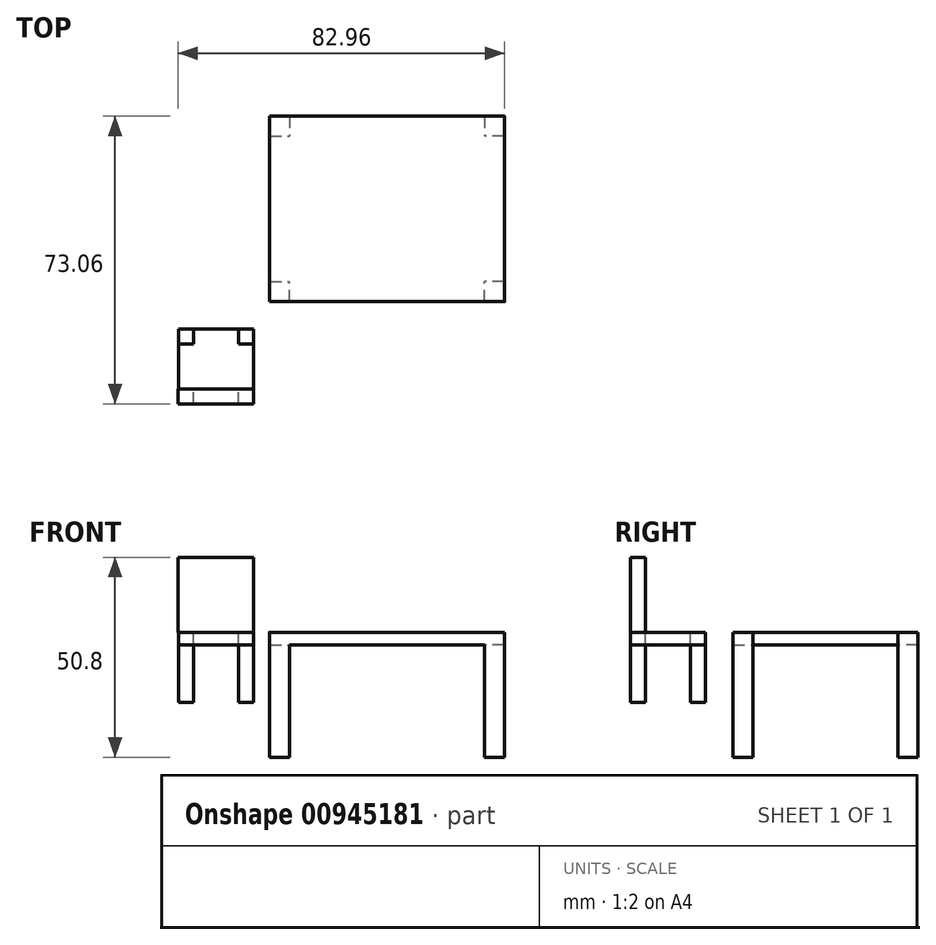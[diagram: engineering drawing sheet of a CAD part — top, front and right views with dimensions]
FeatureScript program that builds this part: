
annotation { "Feature Type Name" : "Feature", "Feature Type Description" : "" }
export const myFeature = defineFeature(function(context is Context, id is Id, definition is map)
    precondition{}
    {
        {
            var Q0;
            Q0=qCreatedBy(makeId("Top.planeOp"),FACE);
            var sketch = newSketch(context, id + "F0", { "sketchPlane" : qUnion([Q0])});
            skLineSegment(sketch, "E0.bottom", {"start": v(-29.83, 23.55) * mm, "end": v(29.83, 23.55) * mm});
            skLineSegment(sketch, "E0.top", {"start": v(-29.83, -23.55) * mm, "end": v(29.83, -23.55) * mm});
            skLineSegment(sketch, "E0.left", {"start": v(-29.83, 23.55) * mm, "end": v(-29.83, -23.55) * mm});
            skLineSegment(sketch, "E0.right", {"start": v(29.83, 23.55) * mm, "end": v(29.83, -23.55) * mm});
            skPoint(sketch, "E0.middle", {"position": v(0, 0) * mm});
            skSolve(sketch);
        }
        {
            var Q0;
            Q0=makeQuery(id+"F0.imprint","IMPRINT",FACE,{"disambiguationData":[TD([[makeQuery(id+"F0.imprint","IMPRINT",EDGE,{"derivedFrom":sQuery(id+"F0.wireOp",EDGE,"E0.bottom")}),-1.0]])]});
            extrude(context, id + "F1", {"entities" : qUnion([Q0]), "depth" : -3.17 * mm, "offsetDistance" : 25.4 * mm});
        }
        {
            var Q0;
            Q0=qCreatedBy(makeId("Top.planeOp"),FACE);
            var sketch = newSketch(context, id + "F2", { "sketchPlane" : qUnion([Q0])});
            skLineSegment(sketch, "E1.bottom", {"start": v(29.87, -23.54) * mm, "end": v(24.79, -23.54) * mm});
            skLineSegment(sketch, "E1.top", {"start": v(29.87, -18.46) * mm, "end": v(24.79, -18.46) * mm});
            skLineSegment(sketch, "E1.left", {"start": v(29.87, -23.54) * mm, "end": v(29.87, -18.46) * mm});
            skLineSegment(sketch, "E1.right", {"start": v(24.79, -23.54) * mm, "end": v(24.79, -18.46) * mm});
            skLineSegment(sketch, "E2.MirrorCS", {"start": v(29.87, 23.54) * mm, "end": v(24.79, 23.54) * mm});
            skLineSegment(sketch, "E3.MirrorCS", {"start": v(24.79, 23.54) * mm, "end": v(24.79, 18.46) * mm});
            skLineSegment(sketch, "E4.MirrorCS", {"start": v(29.87, 18.46) * mm, "end": v(24.79, 18.46) * mm});
            skLineSegment(sketch, "E5.MirrorCS", {"start": v(29.87, 23.54) * mm, "end": v(29.87, 18.46) * mm});
            skLineSegment(sketch, "E6.MirrorCS", {"start": v(-24.79, 23.54) * mm, "end": v(-24.79, 18.46) * mm});
            skLineSegment(sketch, "E7.MirrorCS", {"start": v(-29.87, 18.46) * mm, "end": v(-24.79, 18.46) * mm});
            skLineSegment(sketch, "E8.MirrorCS", {"start": v(-29.87, 23.54) * mm, "end": v(-29.87, 18.46) * mm});
            skLineSegment(sketch, "E9.MirrorCS", {"start": v(-29.87, 23.54) * mm, "end": v(-24.79, 23.54) * mm});
            skLineSegment(sketch, "E10.MirrorCS", {"start": v(-24.79, -23.54) * mm, "end": v(-24.79, -18.46) * mm});
            skLineSegment(sketch, "E11.MirrorCS", {"start": v(-29.87, -23.54) * mm, "end": v(-24.79, -23.54) * mm});
            skLineSegment(sketch, "E12.MirrorCS", {"start": v(-29.87, -23.54) * mm, "end": v(-29.87, -18.46) * mm});
            skLineSegment(sketch, "E13.MirrorCS", {"start": v(-29.87, -18.46) * mm, "end": v(-24.79, -18.46) * mm});
            skSolve(sketch);
        }
        {
            var Q0;
            Q0=makeQuery(id+"F2.imprint","IMPRINT",FACE,{"disambiguationData":[TD([[makeQuery(id+"F2.imprint","IMPRINT",EDGE,{"derivedFrom":sQuery(id+"F2.wireOp",EDGE,"E6.MirrorCS")}),-1.0]])]});
            var Q1;
            Q1=makeQuery(id+"F2.imprint","IMPRINT",FACE,{"disambiguationData":[TD([[makeQuery(id+"F2.imprint","IMPRINT",EDGE,{"derivedFrom":sQuery(id+"F2.wireOp",EDGE,"E10.MirrorCS")}),1.0]])]});
            var Q2;
            Q2=makeQuery(id+"F2.imprint","IMPRINT",FACE,{"disambiguationData":[TD([[makeQuery(id+"F2.imprint","IMPRINT",EDGE,{"derivedFrom":sQuery(id+"F2.wireOp",EDGE,"E1.bottom")}),-1.0]])]});
            var Q3;
            Q3=makeQuery(id+"F2.imprint","IMPRINT",FACE,{"disambiguationData":[TD([[makeQuery(id+"F2.imprint","IMPRINT",EDGE,{"derivedFrom":sQuery(id+"F2.wireOp",EDGE,"E2.MirrorCS")}),1.0]])]});
            extrude(context, id + "F3", {"entities" : qUnion([Q0, Q1, Q2, Q3]), "operationType" : NewBodyOperationType.ADD, "depth" : -31.75 * mm, "offsetDistance" : 25.4 * mm});
        }
        {
            var Q0;
            Q0=qCreatedBy(makeId("Top.planeOp"),FACE);
            var sketch = newSketch(context, id + "F4", { "sketchPlane" : qUnion([Q0])});
            skLineSegment(sketch, "E14.bottom", {"start": v(-52.96, -30.46) * mm, "end": v(-33.91, -30.46) * mm});
            skLineSegment(sketch, "E14.top", {"start": v(-52.96, -49.51) * mm, "end": v(-33.91, -49.51) * mm});
            skLineSegment(sketch, "E14.left", {"start": v(-52.96, -30.46) * mm, "end": v(-52.96, -49.51) * mm});
            skLineSegment(sketch, "E14.right", {"start": v(-33.91, -30.46) * mm, "end": v(-33.91, -49.51) * mm});
            skSolve(sketch);
        }
        {
            var Q0;
            Q0=qCreatedBy(makeId("Top.planeOp"),FACE);
            var sketch = newSketch(context, id + "F5", { "sketchPlane" : qUnion([Q0])});
            skLineSegment(sketch, "E15.bottom", {"start": v(-52.95, -34.27) * mm, "end": v(-49.14, -34.27) * mm});
            skLineSegment(sketch, "E15.top", {"start": v(-52.95, -30.46) * mm, "end": v(-49.14, -30.46) * mm});
            skLineSegment(sketch, "E15.left", {"start": v(-52.95, -34.27) * mm, "end": v(-52.95, -30.46) * mm});
            skLineSegment(sketch, "E15.right", {"start": v(-49.14, -34.27) * mm, "end": v(-49.14, -30.46) * mm});
            skLineSegment(sketch, "E16.MirrorCS", {"start": v(-49.14, -49.5) * mm, "end": v(-52.95, -49.5) * mm});
            skLineSegment(sketch, "E17.MirrorCS", {"start": v(-49.14, -49.5) * mm, "end": v(-49.14, -45.69) * mm});
            skLineSegment(sketch, "E18.MirrorCS", {"start": v(-52.95, -49.5) * mm, "end": v(-52.95, -45.69) * mm});
            skLineSegment(sketch, "E19.MirrorCS", {"start": v(-49.14, -45.69) * mm, "end": v(-52.95, -45.69) * mm});
            skLineSegment(sketch, "E20.MirrorCS", {"start": v(-33.92, -49.5) * mm, "end": v(-37.73, -49.5) * mm});
            skLineSegment(sketch, "E21.MirrorCS", {"start": v(-33.92, -49.5) * mm, "end": v(-33.92, -45.69) * mm});
            skLineSegment(sketch, "E22.MirrorCS", {"start": v(-37.73, -49.5) * mm, "end": v(-37.73, -45.69) * mm});
            skLineSegment(sketch, "E23.MirrorCS", {"start": v(-33.92, -45.69) * mm, "end": v(-37.73, -45.69) * mm});
            skLineSegment(sketch, "E24.MirrorCS", {"start": v(-37.73, -30.46) * mm, "end": v(-33.92, -30.46) * mm});
            skLineSegment(sketch, "E25.MirrorCS", {"start": v(-37.73, -34.27) * mm, "end": v(-33.92, -34.27) * mm});
            skLineSegment(sketch, "E26.MirrorCS", {"start": v(-37.73, -34.27) * mm, "end": v(-37.73, -30.46) * mm});
            skLineSegment(sketch, "E27.MirrorCS", {"start": v(-33.92, -34.27) * mm, "end": v(-33.92, -30.46) * mm});
            skSolve(sketch);
        }
        {
            var Q0;
            Q0 = qSketchRegion(id + "F5", true);
            extrude(context, id + "F6", {"entities" : qUnion([Q0]), "depth" : -17.78 * mm, "offsetDistance" : 25.4 * mm});
        }
        {
            var Q0;
            Q0=makeQuery(id+"F4.imprint","IMPRINT",FACE,{"disambiguationData":[TD([[makeQuery(id+"F4.imprint","IMPRINT",EDGE,{"derivedFrom":sQuery(id+"F4.wireOp",EDGE,"E14.bottom")}),-1.0]])]});
            extrude(context, id + "F7", {"entities" : qUnion([Q0]), "depth" : -3.17 * mm, "offsetDistance" : 25.4 * mm});
        }
        {
            var Q0;
            Q0=qCreatedBy(makeId("Top.planeOp"),FACE);
            var sketch = newSketch(context, id + "F8", { "sketchPlane" : qUnion([Q0])});
            skLineSegment(sketch, "E28.bottom", {"start": v(-53.09, -45.76) * mm, "end": v(-33.94, -45.76) * mm});
            skLineSegment(sketch, "E28.top", {"start": v(-53.09, -49.51) * mm, "end": v(-33.94, -49.51) * mm});
            skLineSegment(sketch, "E28.left", {"start": v(-53.09, -45.76) * mm, "end": v(-53.09, -49.51) * mm});
            skLineSegment(sketch, "E28.right", {"start": v(-33.94, -45.76) * mm, "end": v(-33.94, -49.51) * mm});
            skSolve(sketch);
        }
        {
            var Q0;
            Q0 = qSketchRegion(id + "F8", true);
            extrude(context, id + "F9", {"entities" : qUnion([Q0]), "depth" : 19.05 * mm, "offsetDistance" : 25.4 * mm});
        }
    });
